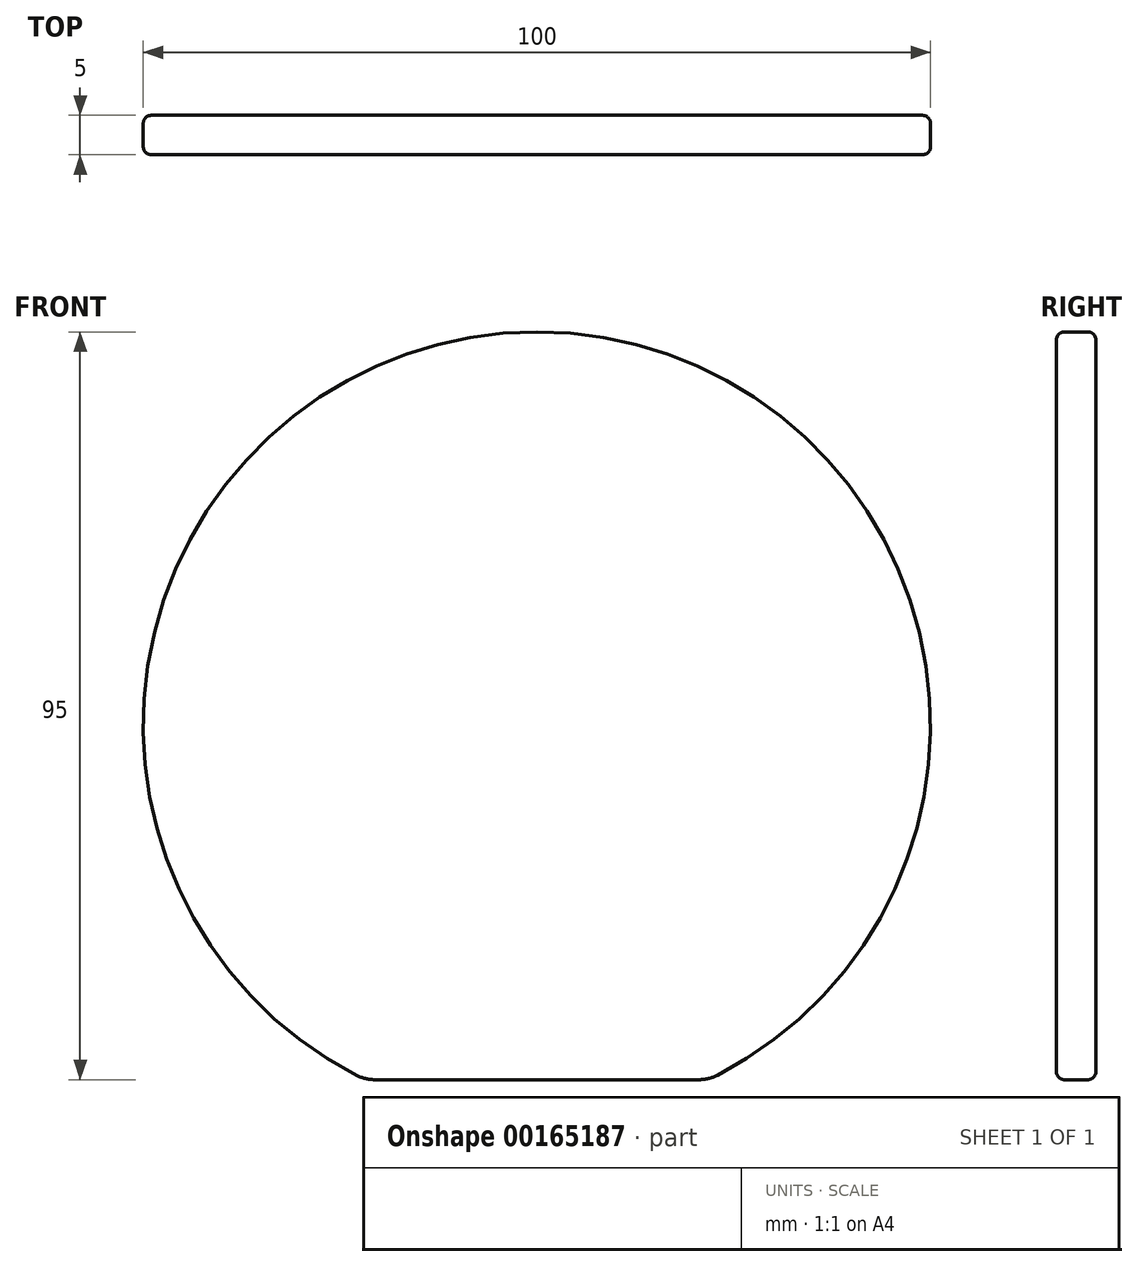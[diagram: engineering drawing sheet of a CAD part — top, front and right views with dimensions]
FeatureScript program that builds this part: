
annotation { "Feature Type Name" : "Feature", "Feature Type Description" : "" }
export const myFeature = defineFeature(function(context is Context, id is Id, definition is map)
    precondition{}
    {
        {
            var Q0;
            Q0=qCreatedBy(makeId("Front.planeOp"),FACE);
            var sketch = newSketch(context, id + "F0", { "sketchPlane" : qUnion([Q0])});
            skArc(sketch, "E0", {"start": v(21.8, -45) * mm, "mid": v(0, 50) * mm, "end": v(-21.8, -45) * mm});
            skLineSegment(sketch, "E1", {"start": v(-21.8, -45) * mm, "end": v(21.8, -45) * mm});
            skSolve(sketch);
        }
        {
            var Q0;
            Q0 = qSketchRegion(id + "F0", true);
            extrude(context, id + "F1", {"entities" : qUnion([Q0]), "depth" : 5 * mm});
        }
        {
            var Q0;
            {var subQ0=sQuery(id+"F0.wireOp",EDGE,"E1");var subQ1=sQuery(id+"F0.wireOp",EDGE,"E0");Q0=makeQuery(id+"F1.opExtrude","SWEPT_EDGE",EDGE,{"disambiguationData":[OSD([subQ1,subQ0]),TDD([makeQuery(id+"F0.imprint","INTERSECT",VERTEX,{"disambiguationData":[OD(0.0)],"derivedFrom":[subQ1,subQ0]})])]});}
            var Q1;
            {var subQ0=sQuery(id+"F0.wireOp",EDGE,"E1");var subQ1=sQuery(id+"F0.wireOp",EDGE,"E0");Q1=makeQuery(id+"F1.opExtrude","SWEPT_EDGE",EDGE,{"disambiguationData":[OSD([subQ1,subQ0]),TDD([makeQuery(id+"F0.imprint","INTERSECT",VERTEX,{"disambiguationData":[OD(1.0)],"derivedFrom":[subQ1,subQ0]})])]});}
            fillet(context, id + "F2", {"entities" : qUnion([Q0, Q1]), "radius" : 5 * mm, "tangentPropagation" : true, "allowEdgeOverflow" : false});
        }
        {
            var Q0;
            Q0=makeQuery(id+"F1.opExtrude","CAP_EDGE",EDGE,{"disambiguationData":[OSD([sQuery(id+"F0.wireOp",EDGE,"E0")])],"isStart":false});
            var Q1;
            Q1=makeQuery(id+"F1.opExtrude","CAP_EDGE",EDGE,{"disambiguationData":[OSD([sQuery(id+"F0.wireOp",EDGE,"E0")])],"isStart":true});
            var Q2;
            Q2=makeQuery(id+"F1.opExtrude","CAP_EDGE",EDGE,{"disambiguationData":[OSD([sQuery(id+"F0.wireOp",EDGE,"E1")])],"isStart":false});
            var Q3;
            Q3=makeQuery(id+"F1.opExtrude","CAP_EDGE",EDGE,{"disambiguationData":[OSD([sQuery(id+"F0.wireOp",EDGE,"E1")])],"isStart":true});
            fillet(context, id + "F3", {"entities" : qUnion([Q0, Q1, Q2, Q3]), "radius" : 1 * mm, "tangentPropagation" : true, "allowEdgeOverflow" : false});
        }
    });
